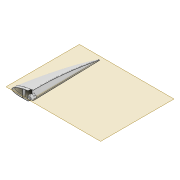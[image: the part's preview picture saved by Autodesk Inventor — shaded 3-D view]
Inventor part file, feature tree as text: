
AUTODESK INVENTOR PART (.ipt)
format: ipt  version: 2022 (Build 260153000, 153)  size: 677,888 bytes
history: native  units: mm
features: sketch x9, extrude x8, plane x4, projected_geometry x2, loft x1, shell x1, fillet x1
ambient origin geometry x8: Origin, YZ Plane, XZ Plane, XY Plane, X Axis, Y Axis, Z Axis, Center Point
bodies: Body1 (feature_tree)
feature tree (26):
  plane  "Work Plane7"
  sketch  "Sketch3"  dims[d45=-250.0mm d46=70.0mm d47=1.0mm d48=5.0mm]
  plane  "Work Plane6"
  sketch  "Sketch17"  dims[d68=0.0mm d69=90.0deg d70=0.0mm d71=90.0deg]
  sketch  "Sketch18"  dims[d72=0.0mm d73=90.0deg d74=0.0mm d75=90.0deg]
  plane  "Work Plane8"
  loft  "Loft4"
  shell  "Shell3"  Thickness=5.0mm
  plane  "Work Plane10"
  sketch  "Sketch32"  dims[d104=66.0mm d122=0.5mm d123=0.0mm]
  extrude  "Extrusion19"  TaperAngle=0.0deg  [1 undecoded]
  extrude  "Extrusion20"  TaperAngle=0.0deg  [1 undecoded]
  sketch  "Sketch36"  dims[d124=0.5mm d125=0.0mm d135=9.8mm]
  extrude  "Extrusion24"  Depth=1.0mm
  extrude  "Extrusion25"  Depth=0.5mm TaperAngle=0.0deg
  extrude  "Extrusion26"  Depth=9.8mm
  extrude  "Extrusion27"  Depth=12.2mm
  extrude  "Extrusion28"  Depth=1.0mm TaperAngle=0.0deg
  fillet  "Fillet4"  Radius=1.5mm
  extrude  "Extrusion31"  Depth=10.0mm TaperAngle=0.0deg
  sketch  "Sketch19"  dims[d76=0.0mm d77=90.0deg d78=1.0mm]
  sketch  "Sketch37"  dims[d136=4.15mm d137=12.2mm]
  sketch  "Sketch38"  dims[d138=2.0mm d139=1.0mm d140=0.0mm d141=1.5mm]
  sketch  "Sketch41"  dims[d142=12.0mm d143=0.0mm d144=10.0mm d145=0.0mm d146=2.1mm d147=6.0mm d148=100.0mm d149=0.0mm d152=8.0mm d153=0.0mm d154=5.0mm d158=2.3mm d159=4.3mm d160=1.15mm d170=3.0mm d171=3.0mm d172=40.0mm d173=1.0mm d174=4.0mm d175=10.0mm d176=0.0mm]
  projected_geometry  "Projected Loop14"
  projected_geometry  "Project Cut Edges5"
note: 2 required parameter values undecoded (feature->parameter linkage not recoverable at this tier; creation-order binding heuristic only, values carry confidence <= 0.55)
